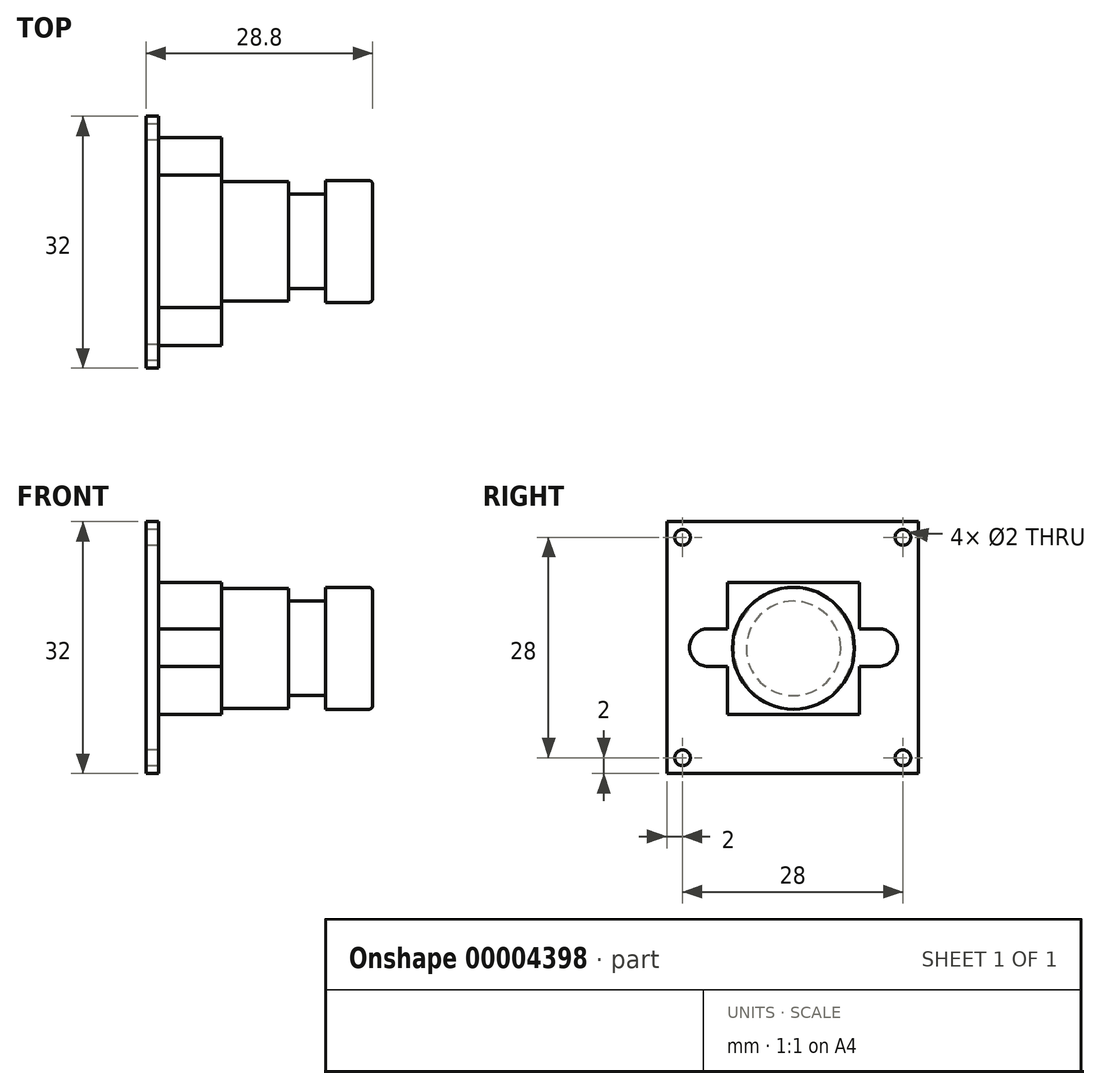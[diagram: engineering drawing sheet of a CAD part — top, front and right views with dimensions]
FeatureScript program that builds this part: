
annotation { "Feature Type Name" : "Feature", "Feature Type Description" : "" }
export const myFeature = defineFeature(function(context is Context, id is Id, definition is map)
    precondition{}
    {
        {
            var Q0;
            Q0=qCreatedBy(makeId("Right.planeOp"),FACE);
            var sketch = newSketch(context, id + "F0", { "sketchPlane" : qUnion([Q0])});
            skLineSegment(sketch, "E0.bottom", {"start": v(0, 0) * mm, "end": v(32, 0) * mm});
            skLineSegment(sketch, "E0.top", {"start": v(0, 32) * mm, "end": v(32, 32) * mm});
            skLineSegment(sketch, "E0.left", {"start": v(0, 0) * mm, "end": v(0, 32) * mm});
            skLineSegment(sketch, "E0.right", {"start": v(32, 0) * mm, "end": v(32, 32) * mm});
            skSolve(sketch);
        }
        {
            var Q0;
            Q0=makeQuery(id+"F0.imprint","IMPRINT",FACE,{"disambiguationData":[TD([[makeQuery(id+"F0.imprint","IMPRINT",EDGE,{"derivedFrom":sQuery(id+"F0.wireOp",EDGE,"E0.bottom")}),1.0]])]});
            extrude(context, id + "F1", {"entities" : qUnion([Q0]), "depth" : 1.6 * mm});
        }
        {
            var Q0;
            Q0=makeQuery(id+"F1.opExtrude","CAP_FACE",FACE,{"disambiguationData":[OSD([sQuery(id+"F0.wireOp",EDGE,"E0.bottom"),sQuery(id+"F0.wireOp",EDGE,"E0.top"),sQuery(id+"F0.wireOp",EDGE,"E0.left"),sQuery(id+"F0.wireOp",EDGE,"E0.right")])],"isStart":false});
            var sketch = newSketch(context, id + "F2", { "sketchPlane" : qUnion([Q0])});
            skLineSegment(sketch, "E1.0", {"start": v(7.7, 7.5) * mm, "end": v(24.5, 7.5) * mm});
            skLineSegment(sketch, "E2.0", {"start": v(7.7, 24.3) * mm, "end": v(24.5, 24.3) * mm});
            skLineSegment(sketch, "E3.0", {"start": v(24.5, 7.5) * mm, "end": v(24.5, 13.6) * mm});
            skLineSegment(sketch, "E4.0", {"start": v(7.7, 7.5) * mm, "end": v(7.7, 13.6) * mm});
            skLineSegment(sketch, "E5.0", {"start": v(5.3, 13.6) * mm, "end": v(7.7, 13.6) * mm});
            skLineSegment(sketch, "E6.0", {"start": v(5.3, 18.4) * mm, "end": v(7.7, 18.4) * mm});
            skArc(sketch, "E7", {"start": v(5.3, 18.4) * mm, "mid": v(2.9, 16) * mm, "end": v(5.3, 13.6) * mm});
            skArc(sketch, "E8", {"start": v(26.9, 13.6) * mm, "mid": v(29.3, 16) * mm, "end": v(26.9, 18.4) * mm});
            skPoint(sketch, "E9.start.orphan", {"position": v(0, 16) * mm});
            skLineSegment(sketch, "E10.trimOffspring", {"start": v(7.7, 18.4) * mm, "end": v(7.7, 24.3) * mm});
            skPoint(sketch, "E11.orphan", {"position": v(32, 16) * mm});
            skLineSegment(sketch, "E12.trimOffspring", {"start": v(24.5, 18.4) * mm, "end": v(24.5, 24.3) * mm});
            skLineSegment(sketch, "E13.trimOffspring", {"start": v(24.5, 13.6) * mm, "end": v(26.9, 13.6) * mm});
            skLineSegment(sketch, "E14.trimOffspring", {"start": v(24.5, 18.4) * mm, "end": v(26.9, 18.4) * mm});
            skSolve(sketch);
        }
        {
            var Q0;
            Q0=makeQuery(id+"F2.imprint","IMPRINT",FACE,{"disambiguationData":[TD([[makeQuery(id+"F2.imprint","IMPRINT",EDGE,{"derivedFrom":sQuery(id+"F2.wireOp",EDGE,"E1.0")}),1.0]])]});
            extrude(context, id + "F3", {"entities" : qUnion([Q0]), "operationType" : NewBodyOperationType.ADD, "depth" : 8 * mm});
        }
        {
            var Q0;
            Q0=makeQuery(id+"F3.opExtrude","CAP_FACE",FACE,{"disambiguationData":[OSD([sQuery(id+"F2.wireOp",EDGE,"E1.0"),sQuery(id+"F2.wireOp",EDGE,"E2.0"),sQuery(id+"F2.wireOp",EDGE,"E3.0"),sQuery(id+"F2.wireOp",EDGE,"E4.0"),sQuery(id+"F2.wireOp",EDGE,"E5.0"),sQuery(id+"F2.wireOp",EDGE,"E6.0"),sQuery(id+"F2.wireOp",EDGE,"E7"),sQuery(id+"F2.wireOp",EDGE,"E8"),sQuery(id+"F2.wireOp",EDGE,"E10.trimOffspring"),sQuery(id+"F2.wireOp",EDGE,"E12.trimOffspring"),sQuery(id+"F2.wireOp",EDGE,"E13.trimOffspring"),sQuery(id+"F2.wireOp",EDGE,"E14.trimOffspring")])],"isStart":false});
            var sketch = newSketch(context, id + "F4", { "sketchPlane" : qUnion([Q0])});
            skCircle(sketch, "E15", {"center": v(16.1, 15.9) * mm, "radius": 7.6 * mm});
            skSolve(sketch);
        }
        {
            var Q0;
            Q0=makeQuery(id+"F4.imprint","IMPRINT",FACE,{"disambiguationData":[TD([[makeQuery(id+"F4.imprint","IMPRINT",EDGE,{"derivedFrom":sQuery(id+"F4.wireOp",EDGE,"E15")}),1.0]])]});
            extrude(context, id + "F5", {"entities" : qUnion([Q0]), "operationType" : NewBodyOperationType.ADD, "depth" : 8.5 * mm});
        }
        {
            var Q0;
            Q0=makeQuery(id+"F5.opExtrude","CAP_FACE",FACE,{"disambiguationData":[OSD([sQuery(id+"F4.wireOp",EDGE,"E15")])],"isStart":false});
            var sketch = newSketch(context, id + "F6", { "sketchPlane" : qUnion([Q0])});
            skCircle(sketch, "E16", {"center": v(16.1, 15.9) * mm, "radius": 6 * mm});
            skSolve(sketch);
        }
        {
            var Q0;
            Q0=makeQuery(id+"F6.imprint","IMPRINT",FACE,{"disambiguationData":[TD([[makeQuery(id+"F6.imprint","IMPRINT",EDGE,{"derivedFrom":sQuery(id+"F6.wireOp",EDGE,"E16")}),1.0]])]});
            extrude(context, id + "F7", {"entities" : qUnion([Q0]), "operationType" : NewBodyOperationType.ADD, "depth" : 4.7 * mm});
        }
        {
            var Q0;
            Q0=makeQuery(id+"F7.opExtrude","CAP_FACE",FACE,{"disambiguationData":[OSD([sQuery(id+"F6.wireOp",EDGE,"E16")])],"isStart":false});
            var sketch = newSketch(context, id + "F8", { "sketchPlane" : qUnion([Q0])});
            skCircle(sketch, "E17", {"center": v(16.1, 15.9) * mm, "radius": 7.75 * mm});
            skSolve(sketch);
        }
        {
            var Q0;
            {var subQ0=makeQuery(id+"F8.imprint","IMPRINT",EDGE,{"derivedFrom":makeQuery(id+"F7.opExtrude","CAP_EDGE",EDGE,{"disambiguationData":[OSD([sQuery(id+"F6.wireOp",EDGE,"E16")])],"isStart":false})});Q0=qUnion([makeQuery(id+"F8.imprint","IMPRINT",FACE,{"disambiguationData":[TD([[makeQuery(id+"F8.imprint","IMPRINT",EDGE,{"derivedFrom":sQuery(id+"F8.wireOp",EDGE,"E17")}),1.0]])]}),makeQuery(id+"F8.imprint","IMPRINT",FACE,{"disambiguationData":[TD([[subQ0,1.0]])]})]);}
            extrude(context, id + "F9", {"entities" : qUnion([Q0]), "operationType" : NewBodyOperationType.ADD, "depth" : 6 * mm});
        }
        {
            var Q0;
            Q0=makeQuery(id+"F9.opExtrude","CAP_EDGE",EDGE,{"disambiguationData":[OSD([sQuery(id+"F8.wireOp",EDGE,"E17")])],"isStart":false});
            fillet(context, id + "F10", {"entities" : qUnion([Q0]), "radius" : 0.5 * mm, "tangentPropagation" : true, "allowEdgeOverflow" : false});
        }
        {
            var Q0;
            Q0=makeQuery(id+"F1.opExtrude","CAP_FACE",FACE,{"disambiguationData":[OSD([sQuery(id+"F0.wireOp",EDGE,"E0.bottom"),sQuery(id+"F0.wireOp",EDGE,"E0.top"),sQuery(id+"F0.wireOp",EDGE,"E0.left"),sQuery(id+"F0.wireOp",EDGE,"E0.right")])],"isStart":true});
            var sketch = newSketch(context, id + "F11", { "sketchPlane" : qUnion([Q0])});
            skCircle(sketch, "E18", {"center": v(-30, 30) * mm, "radius": 1 * mm});
            skCircle(sketch, "E19", {"center": v(-2, 30) * mm, "radius": 1 * mm});
            skCircle(sketch, "E20", {"center": v(-30, 2) * mm, "radius": 1 * mm});
            skCircle(sketch, "E21", {"center": v(-2, 2) * mm, "radius": 1 * mm});
            skSolve(sketch);
        }
        {
            var Q0;
            {Q0=qUnion([makeQuery(id+"F11.imprint","IMPRINT",FACE,{"disambiguationData":[TD([[makeQuery(id+"F11.imprint","IMPRINT",EDGE,{"derivedFrom":sQuery(id+"F11.wireOp",EDGE,"E18")}),1.0]])]}),makeQuery(id+"F11.imprint","IMPRINT",FACE,{"disambiguationData":[TD([[makeQuery(id+"F11.imprint","IMPRINT",EDGE,{"derivedFrom":sQuery(id+"F11.wireOp",EDGE,"E19")}),1.0]])]}),makeQuery(id+"F11.imprint","IMPRINT",FACE,{"disambiguationData":[TD([[makeQuery(id+"F11.imprint","IMPRINT",EDGE,{"derivedFrom":sQuery(id+"F11.wireOp",EDGE,"E20")}),1.0]])]}),makeQuery(id+"F11.imprint","IMPRINT",FACE,{"disambiguationData":[TD([[makeQuery(id+"F11.imprint","IMPRINT",EDGE,{"derivedFrom":sQuery(id+"F11.wireOp",EDGE,"E21")}),1.0]])]})]);}
            extrude(context, id + "F12", {"entities" : qUnion([Q0]), "operationType" : NewBodyOperationType.REMOVE, "endBound" : BoundingType.UP_TO_NEXT, "oppositeDirection" : true, "depth" : 25 * mm});
        }
    });
